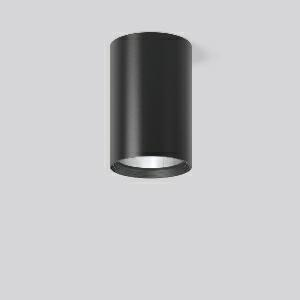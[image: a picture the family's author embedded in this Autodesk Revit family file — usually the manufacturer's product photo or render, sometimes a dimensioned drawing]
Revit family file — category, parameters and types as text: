
# Revit family: heledon_maxi_a_931225_003_f2e5
name_source: partatom
category: Lighting Fixtures
units: mm (PartAtom-declared; Revit-internal decimal feet)

## family parameters
Cut with Voids When Loaded = No
Host = Face
Light Source = No
Part Type = Normal
Room Calculation Point = No
Round Connector Dimension = Use Diameter
Shared = No

## types (1)
- HELEDON maxi A (1 x LED Modul 930, 4350 lm, 3000)
    Apparent Load = 35 VA
    Approval mark = CE
    CIE Flux Codes = 100 100 100 100 100
    Color Rendering = 90
    Color Temperature = 3000
    Default Elevation = 1800 mm
    Description = Series: HELEDON maxi
Cylindrical surface-mounted downlight. Housing: die-cast aluminium, powder-coated. Internal ceiling frame polycarbonate with bayonet mounting. Black plastic ring and recessed LED to prevent glare from the side. Optical assembly with reflector made of MIRO-Silver with 98% total light reflection for outstanding efficiency - can be changed without tools. Best colour rendering index Ra>90. Suitable for Ceiling mounting. Easy installation with a separate ceiling frame with bayonet mounting and plug connection. Driver integrated. Connected via plug-in connector. High quality converter without flickering and stroboscopic effect. The following accessories can be mounted without use of tools: interchangeable lenses, decorative glasses, honeycomb louvre, clear and frosted diffusers, white interchangeable plastic ring. 
Colour: deep black, matt (RAL 9005)
Diameter: 123 mm
Height: 183 mm
Lamp: LED
Socket: without socket
Colour temperature: 3000K
Colour rendering index (CRI): 92
System power: 35 W
Rated luminous flux: 4350 lm
Luminous efficiency: 124 lm/W
Control gear: Regulated power supply
Protection class: I
Type of protection: IP 20
    Height = 183 mm
    Lamp = 1 x LED Modul 930
    Lamp Light Flux = 4350 lm
    Lamp count = 1
    Length = 123 mm
    Lifetime = 50000 h
    Luminous efficacy = 124 lm/W
    Manufacturer = RZB
    ModVariant = No
    Model = 931225.003
    Mounting Place = Ceiling
    Mounting Type = Surface mounted
    Number of Poles = 1
    OnlyDefault = Yes
    Power Factor = 1
    Product Name = HELEDON maxi A
    Product group = Surface mounted downlights
    ProductGroupID = 302
    Protection Class = Protection class I
    Protection Degree = IP 20
    RLX_Detail_Level = 1
    RLX_Emergency_Light_Flux = 0 lm
    RLX_Emergency_Type = 0
    RLX_Emergency_Type_DB = No
    RlxData = <blob elided: 97337 chars, md5=ede86a80>
    Socket = socket
    Standby Power = 0 W
    System Light Flux = 4350 lm
    System Power = 35 W
    Type Comments = Product without accessories
    Type Image = 931192.003.jpg
    URL = http://relux.com
    VarID = ---
    Voltage = 230 V
    Voltage Range = 220-240 V
    Weight = 0.00 kg
    Width = 0 mm  [stored 0 ft]

note: [stored X ft] marks values corroborated as IEEE doubles in the binary element streams (Revit-internal decimal feet)

## geometry (parser evidence)
native form markers: Blend x4, Sweep x12
no freeform markers — native parametric forms only
